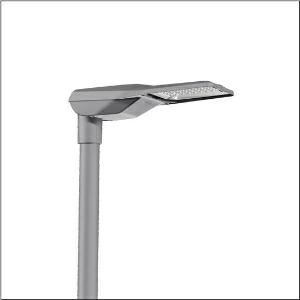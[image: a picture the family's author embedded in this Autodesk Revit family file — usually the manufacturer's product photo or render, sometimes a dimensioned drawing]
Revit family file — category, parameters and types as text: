
# Revit family: streetlight_sl_21_iq_mini___pl52_5xe2h31d08hb_f62b
name_source: partatom
category: Lighting Fixtures
units: mm (PartAtom-declared; Revit-internal decimal feet)

## family parameters
Cut with Voids When Loaded = No
Host = Face
Light Source = No
Part Type = Normal
Room Calculation Point = No
Round Connector Dimension = Use Diameter
Shared = No

## types (1)
- --- (1 x LED, 9290 lm, 70.9 W, 3000K)
    Apparent Load = 71 VA
    CIE Flux Codes = 27 59 98 100 100
    Color Rendering = 70
    Color Temperature = 3000K
    Default Elevation = 1800 mm
    Description = Streetlight SL 21 iQ mini, mast luminaire, primary light control with lens, of PMMA, primary optical cover: cover, of toughened safety glass, transparent, light distribution: PL52, light emission: direct distribution, primary light characteristic: asymmetric, installation type: post-top, side-entry, LED, High Power LED, rated luminous flux: 9.290lm, luminous efficacy: 131lm/W, light colour: 730, colour temperature: 3000K, control: Auto-Match, Temp-Guard, Lumen-Switch, Night-Set, Smart-Wire, Light-Fading, Desk-Remote (wireless, voltage-free reading and setting of iQ features in the workshop via application-optimized NFC function/RFID function), optimised constant luminous flux control (CLO 2.0), pre-setting: linear dimming characteristic, mains connection: 220..240V, AC, 50/60Hz, start of lifetime: 71W, end of service life: 75W, reduction: 31W, luminaire housing, of diecast aluminium, powder-coated, Siteco® metallic grey (DB 702S), corrosivity category C5 mid according to DIN EN ISO 12944, please order mast flange separately, inclination adjustable: 0°, 5°, 10°, 15°, sealing non-destructively replaceable, multi-level sealing system, length: 628mm, width: 235mm, height: 110mm, mast flange for spigot size: 42mm (side-entry): 5XC10008XM4, 60/48mm (side-entry/post-top): 5XC10108XM2, 76/60mm (side-entry/post-top): 5XC10108XM1, protection rating (complete): IP66, insulation class (complete): insulation class II (safety insulation), certification: CE, ENEC, ENEC+, VDE, impact resistance: IK09, permissible operating ambient temperature for outdoor applications: -40..+50°C, standard-compliant lighting for roads and squares, packaging unit: 1 piece

Light Distribution: PL52
    Height = 110 mm
    Lamp = 1 x LED
    Lamp Light Flux = 9290 lm
    Lamp Power = 70.9 W
    Lamp count = 1
    Length = 625 mm
    Luminous efficacy = 131 lm/W
    Manufacturer = Siteco
    ModVariant = No
    Model = 5XE2H31D08HB
    Number of Poles = 1
    OnlyDefault = Yes
    Power Factor = 1
    Product Name = Streetlight SL 21 iQ mini | PL52
    Product group = mast luminaire | pylon top
    ProductGroupID = 6100
    Protection Class = Protection class II
    Protection Degree = IP 66
    RLX_Detail_Level = 1
    RLX_Emergency_Light_Flux = 0 lm
    RLX_Emergency_Type = 0
    RLX_Emergency_Type_DB = No
    RlxData = <blob elided: 101861 chars, md5=2712a37f>
    Socket = socket
    Standby Power = 0 W
    System Light Flux = 9290 lm
    System Power = 71 W
    Type Comments = factory setting: luminous flux: 100 % | dim-lin: 254 | 711 mA
    Type Image = l_1003519.jpg
    URL = http://relux.com
    VarID = @adj_128825
    Voltage = 0 V
    Weight = 0.00 kg
    Width = 234 mm

## geometry (parser evidence)
native form markers: Blend x4, Sweep x9
no freeform markers — native parametric forms only
